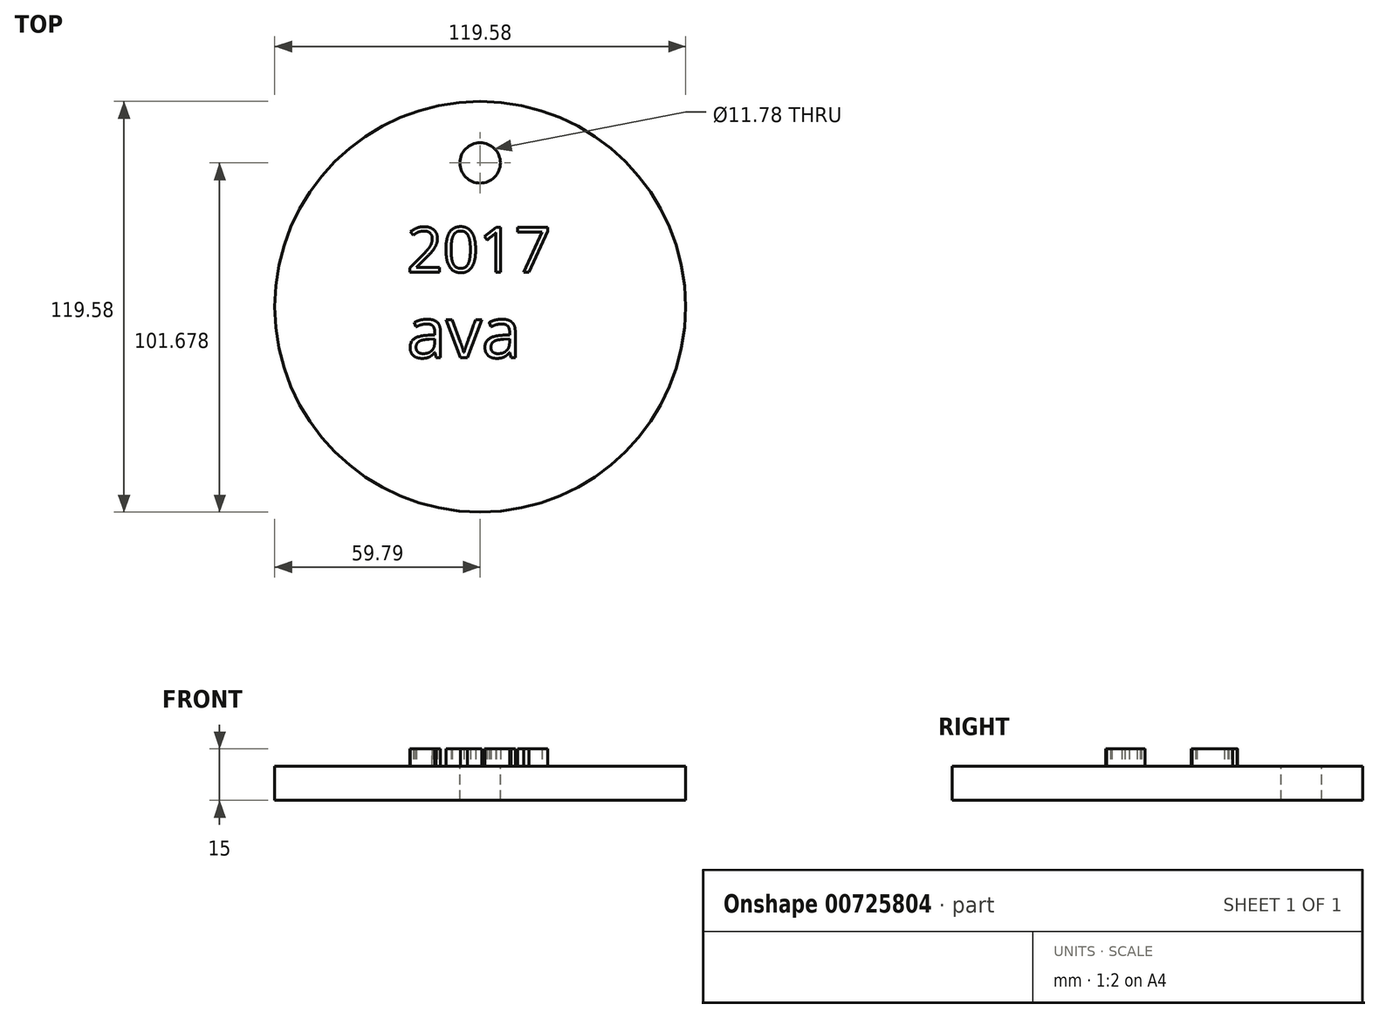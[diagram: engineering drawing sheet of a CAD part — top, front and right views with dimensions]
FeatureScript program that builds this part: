
annotation { "Feature Type Name" : "Feature", "Feature Type Description" : "" }
export const myFeature = defineFeature(function(context is Context, id is Id, definition is map)
    precondition{}
    {
        {
            var Q0;
            Q0=qCreatedBy(makeId("Top.planeOp"),FACE);
            var sketch = newSketch(context, id + "F0", { "sketchPlane" : qUnion([Q0])});
            skCircle(sketch, "E0", {"center": v(0, 0) * mm, "radius": 59.79 * mm});
            skSolve(sketch);
        }
        {
            var Q0;
            Q0=makeQuery(id+"F0.imprint","IMPRINT",FACE,{"disambiguationData":[TD([[makeQuery(id+"F0.imprint","IMPRINT",EDGE,{"derivedFrom":sQuery(id+"F0.wireOp",EDGE,"E0")}),1.0]])]});
            extrude(context, id + "F1", {"entities" : qUnion([Q0]), "depth" : 10 * mm, "offsetDistance" : 25 * mm});
        }
        {
            var Q0;
            Q0=makeQuery(id+"F1.opExtrude","CAP_FACE",FACE,{"disambiguationData":[OSD([sQuery(id+"F0.wireOp",EDGE,"E0")])],"isStart":false});
            var sketch = newSketch(context, id + "F2", { "sketchPlane" : qUnion([Q0])});
            skCircle(sketch, "E1", {"center": v(0, 41.89) * mm, "radius": 5.89 * mm});
            skSolve(sketch);
        }
        {
            var Q0;
            Q0 = qSketchRegion(id + "F2", true);
            extrude(context, id + "F3", {"entities" : qUnion([Q0]), "operationType" : NewBodyOperationType.REMOVE, "oppositeDirection" : true, "depth" : 25 * mm, "offsetDistance" : 25 * mm});
        }
        {
            var Q0;
            Q0=makeQuery(id+"F1.opExtrude","CAP_FACE",FACE,{"disambiguationData":[OSD([sQuery(id+"F0.wireOp",EDGE,"E0")])],"isStart":false});
            var sketch = newSketch(context, id + "F4", { "sketchPlane" : qUnion([Q0])});
            skText(sketch, "E2", { "text": "ava", "fontName": "OpenSans-Regular.ttf"});
            skText(sketch, "E3", { "text": "2017", "fontName": "OpenSans-Regular.ttf"});
            const initialGuessF4  = {"E2": [-0.02135, -0.01484, 1, 0, 0.01484], "E3": [-0.02135, 0.01006, 1, 0, 0.01319]};
            skSetInitialGuess(sketch, initialGuessF4);
            skSolve(sketch);
        }
        {
            var Q0;
            Q0 = qSketchRegion(id + "F4", true);
            extrude(context, id + "F5", {"entities" : qUnion([Q0]), "operationType" : NewBodyOperationType.ADD, "depth" : 5 * mm, "offsetDistance" : 25 * mm});
        }
    });
